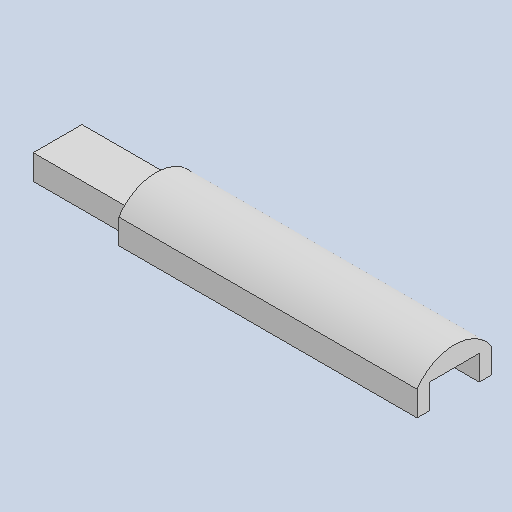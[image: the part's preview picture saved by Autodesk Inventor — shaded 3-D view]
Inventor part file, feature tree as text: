
AUTODESK INVENTOR PART (.ipt)
format: ipt  version: 2023 (Build 270158000, 158)  size: 105,984 bytes
history: native  units: in
note: dims shown in document units (in); Inventor stores cm internally (conversion verified against a paired STEP export)
features: other x3, sketch x3
ambient origin geometry x8: Origin, YZ Plane, XZ Plane, XY Plane, X Axis, Y Axis, Z Axis, Center Point
bodies: Solid1 (feature_tree)
feature tree (6):
  other  "Part_3_hand_extention.ipt"
  other  "Solid1::Part_3_hand_extention.ipt"
  other  "TaggingFeature1"
  sketch  "Sketch1"  dims[d0=0.3937in]
  sketch  "Sketch2"
  sketch  "Sketch3"
